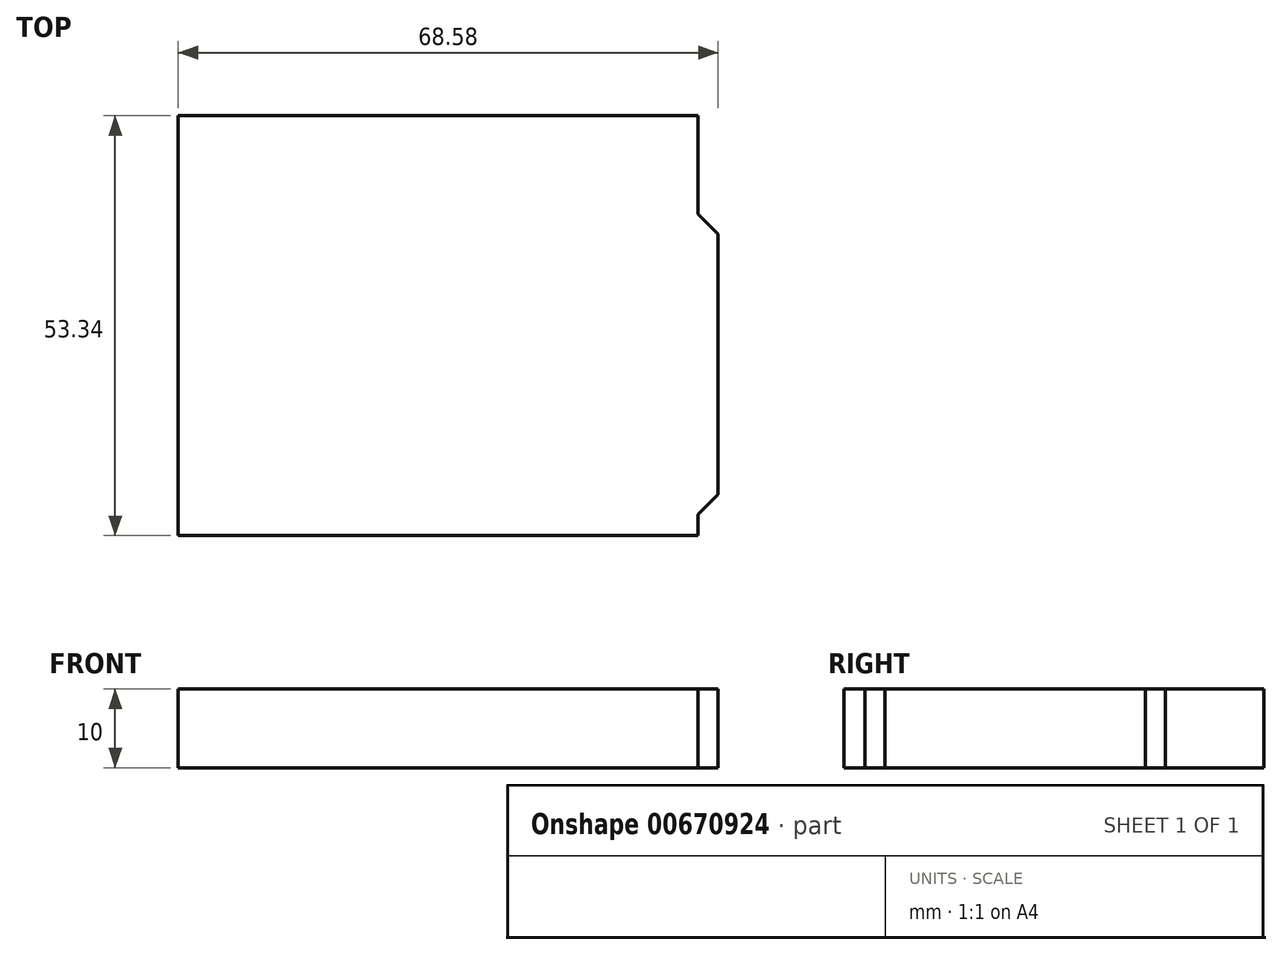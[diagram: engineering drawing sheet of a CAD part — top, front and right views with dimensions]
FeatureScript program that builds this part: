
annotation { "Feature Type Name" : "Feature", "Feature Type Description" : "" }
export const myFeature = defineFeature(function(context is Context, id is Id, definition is map)
    precondition{}
    {
        {
            var Q0;
            Q0=qCreatedBy(makeId("Top.planeOp"),FACE);
            var sketch = newSketch(context, id + "F0", { "sketchPlane" : qUnion([Q0])});
            skLineSegment(sketch, "E0", {"start": v(-33.02, 26.67) * mm, "end": v(33.02, 26.67) * mm});
            skLineSegment(sketch, "E1", {"start": v(33.02, 26.67) * mm, "end": v(33.02, -26.67) * mm});
            skLineSegment(sketch, "E2", {"start": v(-33.02, 26.67) * mm, "end": v(-33.02, -26.67) * mm});
            skLineSegment(sketch, "E3", {"start": v(-33.02, -26.67) * mm, "end": v(33.02, -26.67) * mm});
            skLineSegment(sketch, "E4", {"start": v(0, 0) * mm, "end": v(-33.02, 0) * mm, "construction": true});
            skLineSegment(sketch, "E5", {"start": v(0, 0) * mm, "end": v(0, 26.67) * mm, "construction": true});
            skLineSegment(sketch, "E6", {"start": v(33.02, -24) * mm, "end": v(35.56, -21.46) * mm});
            skLineSegment(sketch, "E7", {"start": v(35.56, -21.46) * mm, "end": v(35.56, 11.6) * mm});
            skLineSegment(sketch, "E8", {"start": v(35.56, 11.6) * mm, "end": v(33.02, 14.15) * mm});
            skSolve(sketch);
        }
        {
            var Q0;
            {var subQ4=sQuery(id+"F0.wireOp",EDGE,"E0");Q0=makeQuery(id+"F0.imprint","IMPRINT",FACE,{"disambiguationData":[TD([[makeQuery(id+"F0.imprint","IMPRINT",EDGE,{"derivedFrom":subQ4}),-1.0]])]});}
            var Q1;
            {var subQ0=sQuery(id+"F0.wireOp",EDGE,"E6");Q1=makeQuery(id+"F0.imprint","IMPRINT",FACE,{"disambiguationData":[TD([[makeQuery(id+"F0.imprint","IMPRINT",EDGE,{"derivedFrom":subQ0}),1.0]])]});}
            extrude(context, id + "F1", {"entities" : qUnion([Q0, Q1]), "depth" : 10 * mm, "offsetDistance" : 25 * mm});
        }
    });
